# Revit family: IS_CerathermNavigo_A7301_BIM_NL
name_source: partatom
category: Plumbing Fixtures
units: mm (PartAtom-declared; Revit-internal decimal feet)

## family parameters
Always vertical = No
Cut with Voids When Loaded = No
OmniClass Number = 23.45.55.17
OmniClass Title = Mixing Faucets
Part Type = Normal
Room Calculation Point = No
Round Connector Dimension = Use Diameter
Shared = No
Work Plane-Based = No

## types (4) — shared parameters
Accesoires = https://www.idealstandard.nl
Accessories = https://www.idealstandard.nl
Afmetingen = 157 x 157 x 44 mm
AfstandsEenheid = Millimeter
AreaUnits = millimeter
Artikelreferentie = Ceratherm Navigo Thermal Shower 1-Control
AssetType = Shower Mixer
Auteur = Ideal Standard
BIMObjectName = IS_IdealStandard_ShowerMixers_CerathermNavigo_A7301
BIMobject category = Taps & Mixers
BIMobject category code = sanitary-taps-mixers
BIMobject main category = Sanitary
BIMobject main category code = sanitary
Beschrijvinggarantie = Herstellergarantie
BimObjectNaam = IS_IdealStandard_ShowerMixers_CerathermNavigo_A7301
Brand = Ideal Standard
Brand url = https://www.idealstandard.nl
Breedte = 157
ConnectionType = Plumbing
CurrencyUnit = €
CurrentRevision = 1
Date of publishing = 01/04/2022
Diepte = 44 mm
Douchebak = No
DurationUnit = years
DuurEenheid = Bar
Edition number = 1
FaucetFunction = Turning Controlers
FaucetOperation = Thermal Shower with turning controllers
FaucetTopDescription = Thermal Shower 1-Control (1 Outlet)Square Escutcheon
FaucetType = Thermal Shower
Features = Thermal Shower 1-Control (1 Outlet)Square Escutcheon
Functiekraanwerk = Duschmischer mit 1 Bedienelementen
Garantieonderdelen = 5
Garantieunits = Jahre
GemaaktOp = 01/04/2022
Help = https://www.idealstandard.nl
Hoogte = 157
Hulp = https://www.idealstandard.nl
IFC Classification = Sanitary Terminal
IfcExportAs = IfcValveType
IfcExportType = FAUCET
Installatieinstructies = https://www.idealstandard.nl
Installation instructions = https://www.idealstandard.nl
InstallationInstructions = https://www.idealstandard.nl
Klepmechanisme = Drehknöpfe
Lengte = 44 mm
LinearUnits = millimeter
MaintenanceInformation = https://www.idealstandard.nl
Manufacturer = Ideal Standard
Manufacturer name = Ideal Standard
ManufacturerURL = https://www.idealstandard.nl
Materiaal = Messing
Material = Verchromtes Messing
Material main = Messing
Merk = Ideal Standard
ModelReference = Ceratherm Navigo Thermal Shower 1-Control
NBS Reference Code = 45-35-70/335
NBS Reference Description = Shower mixers
Name = ShowerMixers_CerathermNavigo_A7301_IdealStandard
NettWeight = 1,57 KG
NominalDepth = 44 mm
NominalHeight = 157 mm  [stored 0.515092 ft]
NominalLength = 44 mm
NominalWidth = 157 mm  [stored 0.515092 ft]
Normen = ShowerMixers_CerathermNavigo_A7301_IdealStandard
OmniClass Code = 23-31- 11 00
OmniClass Description = Faucets
OppervlakteEenheid = Millimeter
PredefinedType = Shower Mixer
Product Guid = 146a769d-15ac-4b52-a7ea-6045e992ab96
Product SKU = A7301
Product certification = https://www.idealstandard.nl
Product data url = https://bimobject.com
Product family = Navigo
Product group = Taps & Mixers
Product name = Ceratherm Navigo  Thermal Shower 1 and Square Escutcheon
Product url = https://www.idealstandard.nl
ProductInformation = https://www.idealstandard.nl
ProductSoort = Duschmischer
Productinformatie = https://www.idealstandard.nl
QR code = http://bimobject.com
Revisie = 1
Shape = Cylindrical
ShowerType = Thermal Shower 1-Control (1 Outlet)Square Escutcheon
Size = 157 x 157 x 44 mm
Space = Internal
SpareParts = https://www.idealstandard.nl
Technical description = https://www.idealstandard.nl
Telefoonnummer = (0228) 521-580
Testdruk = 10 bar
Toepassing = Duschmischer
Typeconnectie = Installation
Typekraanwerk = 2 Bedienknöpfe Duschmischer
UNSPSC Code = 301815
URL = https://www.idealstandard.nl
Uniclass 1.4 Code = L725111
Uniclass 1.4 Description = Taps Mixers
Uniclass 2.0 Code = PR-35-06-82
Uniclass 2.0 Description = Shower  Mixer
Uniclass 2015 Code = Pr_40_20_87_78
Uniclass 2015 Name = Shower manual water supply sets
Uniclass2015Beschrijving = Shower manual water supply sets
Uniclass2015Code = Pr_40_20_87_78
Uniclass2015Referentie = Pr_40_20_87_78
Uniclass2015Title = Shower manual water supply sets
Uniclass2015Version = v1.25
Urlproducent = https://www.idealstandard.nl
ValutaEenheid = €
Versie = 1
Version = 1
VolumeUnits = liters
Volumeunits = Liter
Vorm = Zylinder
WRASURL = https://www.wrasapprovals.co.uk
WarrantyDescription = manufacturer warranty
WarrantyDurationParts = 5
WarrantyDurationUnit = years
Wisselstukken = https://www.idealstandard.nl
Youtube clip = https://www.youtube.com
zero-valued in all types: BrutoGewicht, Nettogewicht, Vervangingskosten

## per-type parameters (varying)
| type | Afwerking | Artikelnummer | Artikelomschrijving | BarCode | Color | Description | Eigenschappen | Finish | GTIN code | Kleur | MainColor | Model | ModelNumber |
| A7301AA - Ceratherm Navigo Thermal Shower 1-Control (1 Outlet)Square Escutcheon -Chrome | Chrom | A7301AA | Ceratherm Navigo Brausethermostat 1-Steuerung (1 Ausgang) Quadratische Rosette -Chrom | 4015413349413 | Chrom | Ceratherm Navigo Brausethermostat 1-Steuerung (1 Ausgang) Quadratische Rosette -Chrom | Brausethermostat 1-Steuerung (1 Ausgang) Quadratische Rosette -Chrom | Chrom | https://4015413349413 | Chrom | Chrome | A7301AA | A7301AA |
| A7301A2 - Ceratherm Navigo Thermal Shower 1-Control (1 Outlet)Square Escutcheon -Brush Gold | Pinsel Gold | A7301A2 | Ceratherm Navigo Brausethermostat 1-Steuerung (1 Ausgang) Quadratische Rosette -Bürste Gold | 4015413349536 | Pinsel Gold | Ceratherm Navigo Brausethermostat 1-Steuerung (1 Ausgang) Quadratische Rosette -Bürste Gold | Brausethermostat 1-Steuerung (1 Ausgang) Quadratische Rosette -Bürste Gold | Pinsel Gold | https://4015413349536 | Pinsel Gold | Brush Gold | A7301A2 | A7301A2 |
| A7301A5 - Ceratherm Navigo Thermal Shower 1-Control (1 Outlet)Square Escutcheon -Magnetic Grey | Magnetisches Grau | A7301A5 | Ceratherm Navigo Thermobrausebatterie 1-Steuerung (1 Ausgang) Quadratische Rosette - Magnetisch Grau | 4015413349574 | Magnetisches Grau | Ceratherm Navigo Thermobrausebatterie 1-Steuerung (1 Ausgang) Quadratische Rosette - Magnetisch Grau | Thermobrausebatterie 1-Steuerung (1 Ausgang) Quadratische Rosette - Magnetisch Grau | Magnetisches Grau | https://4015413349574 | Magnetisches Grau | Magnetic Grey | A7301A5 | A7301A5 |
| A7301GN - Ceratherm Navigo Thermal Shower 1-Control (1 Outlet)Square Escutcheon -Silver Storm | Silberner Sturm | A7301GN | Ceratherm Navigo Brausethermostat 1-Steuerung (1 Ausgang) Quadratische Rosette – Silver Storm | 4015413349499 | Silberner Sturm | Ceratherm Navigo Brausethermostat 1-Steuerung (1 Ausgang) Quadratische Rosette – Silver Storm | Brausethermostat 1-Steuerung (1 Ausgang) Quadratische Rosette – Silver Storm | Silberner Sturm | https://4015413349499 | Silberner Sturm | Silver Storm | A7301GN | A7301GN |

note: [stored X ft] marks values corroborated as IEEE doubles in the binary element streams (Revit-internal decimal feet)

## geometry (parser evidence)
native form markers: Sweep x4
no freeform markers — native parametric forms only
